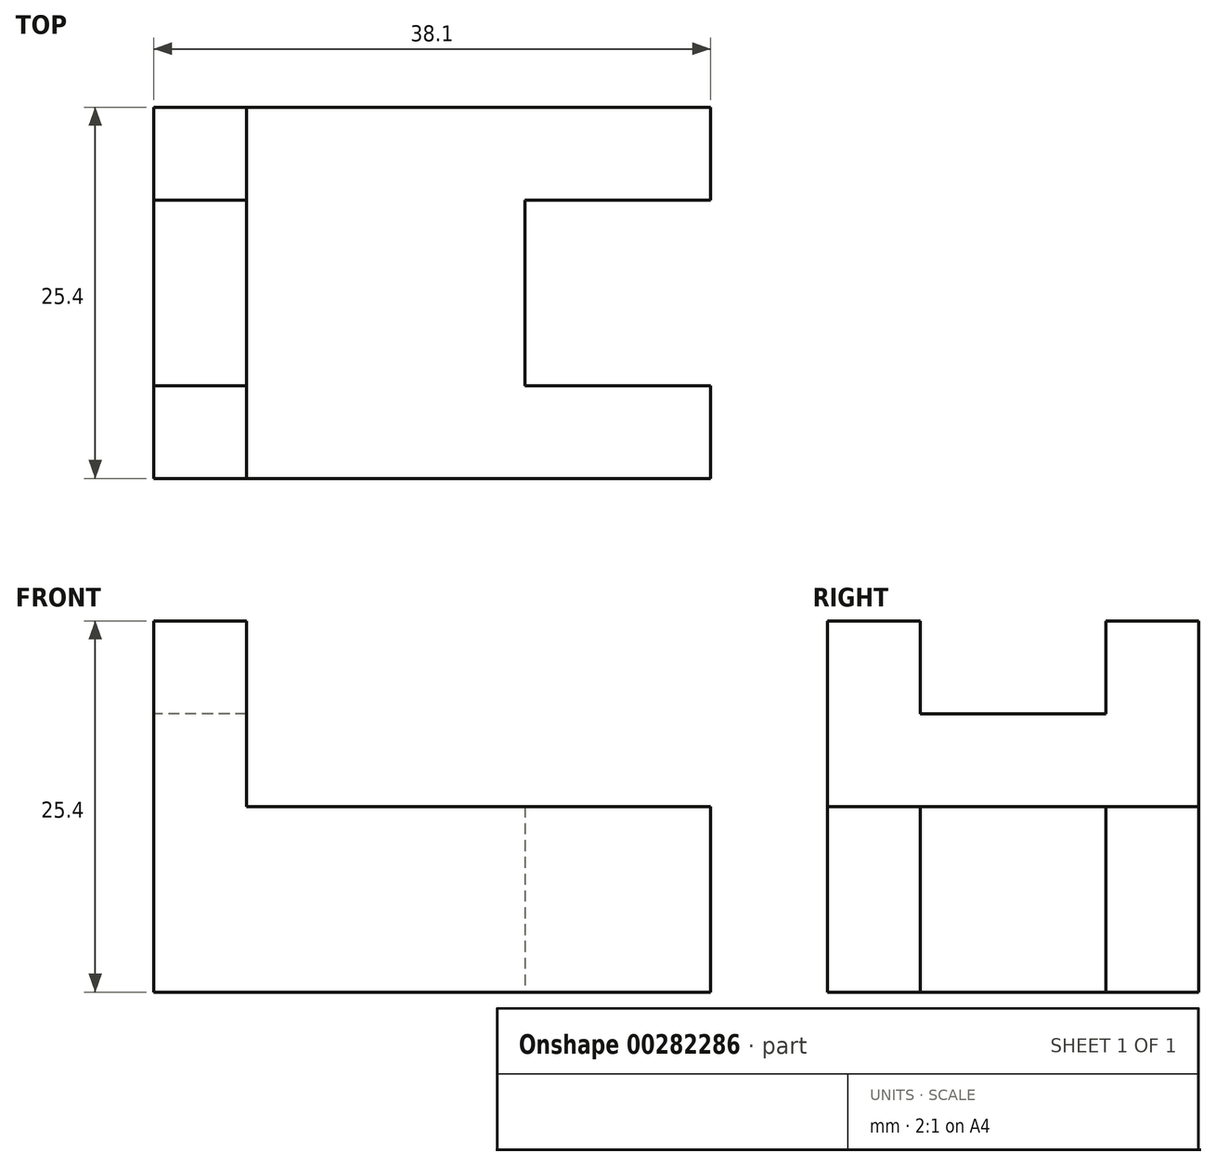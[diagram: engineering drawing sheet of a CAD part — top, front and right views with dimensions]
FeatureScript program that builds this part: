
annotation { "Feature Type Name" : "Feature", "Feature Type Description" : "" }
export const myFeature = defineFeature(function(context is Context, id is Id, definition is map)
    precondition{}
    {
        {
            var Q0;
            Q0=qCreatedBy(makeId("Top.planeOp"),FACE);
            var sketch = newSketch(context, id + "F0", { "sketchPlane" : qUnion([Q0])});
            skLineSegment(sketch, "E0.bottom", {"start": v(0, 0) * mm, "end": v(-25.4, 0) * mm});
            skLineSegment(sketch, "E0.top", {"start": v(0, 25.4) * mm, "end": v(-25.4, 25.4) * mm});
            skLineSegment(sketch, "E0.left", {"start": v(0, 0) * mm, "end": v(0, 25.4) * mm});
            skLineSegment(sketch, "E0.right", {"start": v(-25.4, 0) * mm, "end": v(-25.4, 25.4) * mm});
            skLineSegment(sketch, "E1.bottom", {"start": v(0, 25.4) * mm, "end": v(12.7, 25.4) * mm});
            skLineSegment(sketch, "E1.top", {"start": v(0, 19.05) * mm, "end": v(12.7, 19.05) * mm});
            skLineSegment(sketch, "E1.left", {"start": v(0, 25.4) * mm, "end": v(0, 19.05) * mm});
            skLineSegment(sketch, "E1.right", {"start": v(12.7, 25.4) * mm, "end": v(12.7, 19.05) * mm});
            skLineSegment(sketch, "E2.bottom", {"start": v(0, 0) * mm, "end": v(12.7, 0) * mm});
            skLineSegment(sketch, "E2.top", {"start": v(0, 6.35) * mm, "end": v(12.7, 6.35) * mm});
            skLineSegment(sketch, "E2.left", {"start": v(0, 0) * mm, "end": v(0, 6.35) * mm});
            skLineSegment(sketch, "E2.right", {"start": v(12.7, 0) * mm, "end": v(12.7, 6.35) * mm});
            skSolve(sketch);
        }
        {
            var Q0;
            Q0 = qSketchRegion(id + "F0", true);
            extrude(context, id + "F1", {"entities" : qUnion([Q0]), "depth" : 12.7 * mm});
        }
        {
            var Q0;
            Q0=makeQuery(id+"F1.opExtrude","SWEPT_FACE",FACE,{"disambiguationData":[OSD([sQuery(id+"F0.wireOp",EDGE,"E0.right")])]});
            var sketch = newSketch(context, id + "F2", { "sketchPlane" : qUnion([Q0])});
            skLineSegment(sketch, "E3.bottom", {"start": v(-25.4, 12.7) * mm, "end": v(-19.05, 12.7) * mm});
            skLineSegment(sketch, "E3.top", {"start": v(-25.4, 25.4) * mm, "end": v(-19.05, 25.4) * mm});
            skLineSegment(sketch, "E3.left", {"start": v(-25.4, 12.7) * mm, "end": v(-25.4, 25.4) * mm});
            skLineSegment(sketch, "E3.right", {"start": v(-19.05, 12.7) * mm, "end": v(-19.05, 25.4) * mm});
            skLineSegment(sketch, "E4.bottom", {"start": v(0, 12.7) * mm, "end": v(-6.35, 12.7) * mm});
            skLineSegment(sketch, "E4.top", {"start": v(0, 25.4) * mm, "end": v(-6.35, 25.4) * mm});
            skLineSegment(sketch, "E4.left", {"start": v(0, 12.7) * mm, "end": v(0, 25.4) * mm});
            skLineSegment(sketch, "E4.right", {"start": v(-6.35, 12.7) * mm, "end": v(-6.35, 25.4) * mm});
            skLineSegment(sketch, "E5.bottom", {"start": v(-19.05, 19.05) * mm, "end": v(-6.35, 19.05) * mm});
            skLineSegment(sketch, "E5.top", {"start": v(-19.05, 12.7) * mm, "end": v(-6.35, 12.7) * mm});
            skLineSegment(sketch, "E5.left", {"start": v(-19.05, 19.05) * mm, "end": v(-19.05, 12.7) * mm});
            skLineSegment(sketch, "E5.right", {"start": v(-6.35, 19.05) * mm, "end": v(-6.35, 12.7) * mm});
            skSolve(sketch);
        }
        {
            var Q0;
            Q0 = qSketchRegion(id + "F2", true);
            extrude(context, id + "F3", {"entities" : qUnion([Q0]), "operationType" : NewBodyOperationType.ADD, "oppositeDirection" : true, "depth" : 6.35 * mm});
        }
    });
